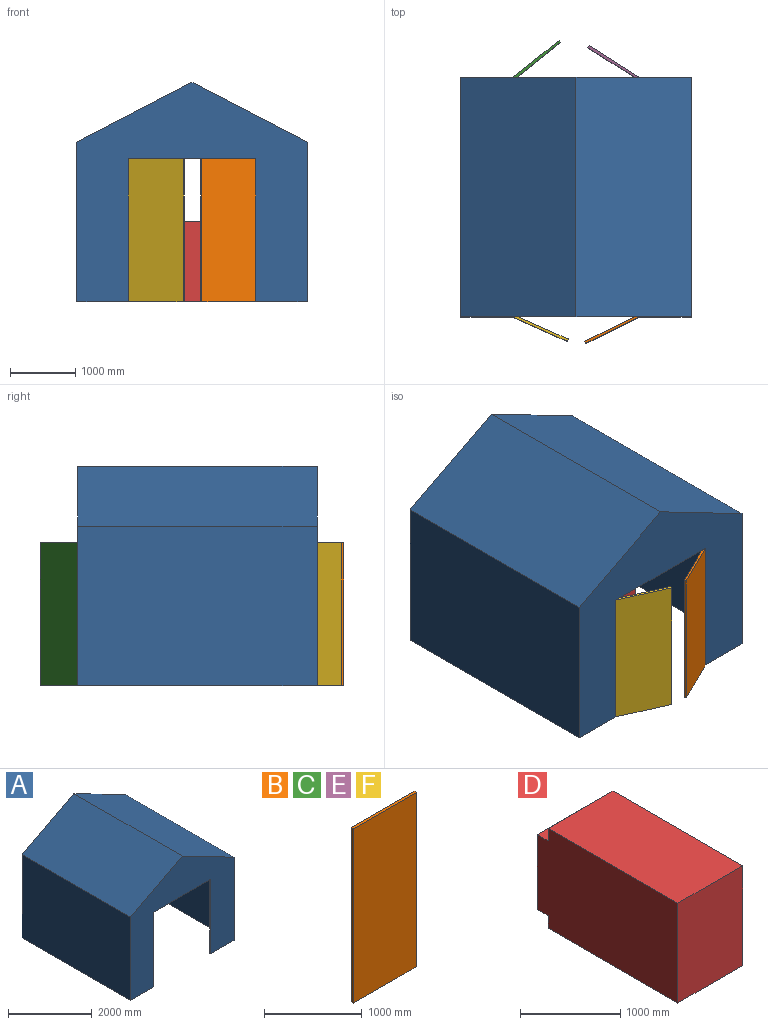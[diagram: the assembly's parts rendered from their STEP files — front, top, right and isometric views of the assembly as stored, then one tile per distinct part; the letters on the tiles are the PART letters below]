
ASSEMBLY  parts=6 mates=8
PART A: 20 faces, bbox 3517.9x3657.6x3352.8 mm
  f0: plane 3657.6x787.4mm, normal (0,0,-1), area 196451.2mm2, adj f1,f2,f3,f4,f9,f13,f16,f17
  f1: plane 3517.9x3352.8mm, normal (0,-1,0), area 5941923.6mm2, adj f0,f5,f6,f7,f8,f9,f17,f18
  f2: plane 3517.9x3352.8mm, normal (0,1,0), area 5941923.6mm2, adj f0,f5,f6,f7,f8,f9,f14,f15
  f3: plane 3441.7x3309.86mm, normal (0,1,0), area 5607573.7mm2, adj f0,f5,f10,f11,f12,f13,f17,f18
  f4: plane 3441.7x3309.86mm, normal (0,-1,0), area 5607573.7mm2, adj f0,f5,f10,f11,f12,f13,f14,f15
  f5: plane 3657.6x787.4mm, normal (0,0,-1), area 196451.2mm2, adj f1,f2,f3,f4,f6,f10,f15,f18
  f6: plane 3657.6x2438.4mm, normal (1,0,0), area 8918691.8mm2, adj f1,f2,f5,f7
  f7: plane 3657.6x1758.95mm, normal (0.46,0,0.89), area 7250939.4mm2, adj f1,f2,f6,f8
  f8: plane 3657.6x1758.95mm, normal (-0.46,0,0.89), area 7250939.4mm2, adj f1,f2,f7,f9
  f9: plane 3657.6x2438.4mm, normal (-1,0,0), area 8918691.8mm2, adj f0,f1,f2,f8
  f10: plane 3581.4x2415.27mm, normal (-1,0,0), area 8650032.8mm2, adj f3,f4,f5,f11
  f11: plane 3581.4x1720.85mm, normal (-0.46,0,-0.89), area 6946090.2mm2, adj f3,f4,f10,f12
  f12: plane 3581.4x1720.85mm, normal (0.46,0,-0.89), area 6946090.2mm2, adj f3,f4,f11,f13
  f13: plane 3581.4x2415.27mm, normal (1,0,0), area 8650032.8mm2, adj f0,f3,f4,f12
  f14: plane 1943.1x38.1mm, normal (0,0,-1), area 74032.1mm2, adj f2,f4,f15,f16
  f15: plane 2184.4x38.1mm, normal (-1,0,0), area 83225.6mm2, adj f2,f4,f5,f14
  f16: plane 2184.4x38.1mm, normal (1,0,0), area 83225.6mm2, adj f0,f2,f4,f14
  f17: plane 2184.4x38.1mm, normal (1,0,0), area 83225.6mm2, adj f0,f1,f3,f19
  f18: plane 2184.4x38.1mm, normal (-1,0,0), area 83225.6mm2, adj f1,f3,f5,f19
  f19: plane 1943.1x38.1mm, normal (0,0,-1), area 74032.1mm2, adj f1,f3,f17,f18
PART B: 6 faces, bbox 914.4x38.1x2184.4 mm
  f0: plane 914.4x38.1mm, normal (0,0,-1), area 34838.6mm2, adj f1,f3,f4,f5
  f1: plane 2184.4x38.1mm, normal (1,0,0), area 83225.6mm2, adj f0,f2,f4,f5
  f2: plane 914.4x38.1mm, normal (0,0,1), area 34838.6mm2, adj f1,f3,f4,f5
  f3: plane 2184.4x38.1mm, normal (-1,0,0), area 83225.6mm2, adj f0,f2,f4,f5
  f4: plane 2184.4x914.4mm, normal (0,-1,0), area 1997415.4mm2, adj f0,f1,f2,f3
  f5: plane 2184.4x914.4mm, normal (0,1,0), area 1997415.4mm2, adj f0,f1,f2,f3
PART C: same geometry as B
PART D: 10 faces, bbox 914.4x1981.2x1219.2 mm
  f0: plane 914.4x152.4mm, normal (0,1,0), area 139354.6mm2, adj f2,f4,f5,f8
  f1: plane 1219.2x914.4mm, normal (0,-1,0), area 1114836.5mm2, adj f2,f4,f5,f6
  f2: plane 1981.2x1219.2mm, normal (1,0,0), area 2369027.5mm2, adj f0,f1,f3,f5,f6,f7,f8,f9
  f3: plane 914.4x152.4mm, normal (0,1,0), area 139354.6mm2, adj f2,f4,f6,f7
  f4: plane 1981.2x1219.2mm, normal (-1,0,0), area 2369027.5mm2, adj f0,f1,f3,f5,f6,f7,f8,f9
  f5: plane 1828.8x914.4mm, normal (0,0,1), area 1672254.7mm2, adj f0,f1,f2,f4
  f6: plane 1828.8x914.4mm, normal (0,0,-1), area 1672254.7mm2, adj f1,f2,f3,f4
  f7: plane 914.4x152.4mm, normal (0,0,-1), area 139354.6mm2, adj f2,f3,f4,f9
  f8: plane 914.4x152.4mm, normal (0,0,1), area 139354.6mm2, adj f0,f2,f4,f9
  f9: plane 914.4x914.4mm, normal (0,1,0), area 836127.4mm2, adj f2,f4,f7,f8
PART E: same geometry as B
PART F: same geometry as B
PLACE A t=(-1758.95,3657.6,1219.2)mm fixed
PLACE B rot(axis=(0,0,1),26.3deg) t=(-1214.16,-168.41,1092.2)mm
PLACE C rot(axis=(0,0,1),38.5deg) t=(-2372.86,3942.43,1092.2)mm
PLACE D t=(-1697.46,1971.93,612.2)mm fixed
PLACE E rot(axis=(0,0,-1),32.5deg) t=(-1173.02,3903.22,1092.2)mm
PLACE F rot(axis=(0,0,-1),24deg) t=(-2297.37,-151.26,1092.2)mm
MATE planar E.f2 <-> A.f14  axis (0,0,1) through (-1183.25,3887.15,2184.4)mm
MATE cylindrical A.f5 <-> E.f0  axis (0,0,1) through (-787.4,3657.6,0)mm
MATE planar C.f2 <-> A.f14  axis (0,0,1) through (-2360.99,3927.52,2184.4)mm
MATE revolute B.f0 <-> A.f5  axis (0,0,1) through (-787.4,0,0)mm
MATE planar A.f19 <-> B.f2  axis (0,0,-1) through (-1758.95,19.05,2184.4)mm
MATE planar A.f19 <-> F.f2  axis (0,0,-1) through (-1758.95,19.05,2184.4)mm
MATE cylindrical C.f0 <-> A.f0  axis (0,0,-1) through (-2730.5,3657.6,0)mm
MATE cylindrical F.f0 <-> A.f0  axis (0,0,1) through (-2730.5,0,0)mm
